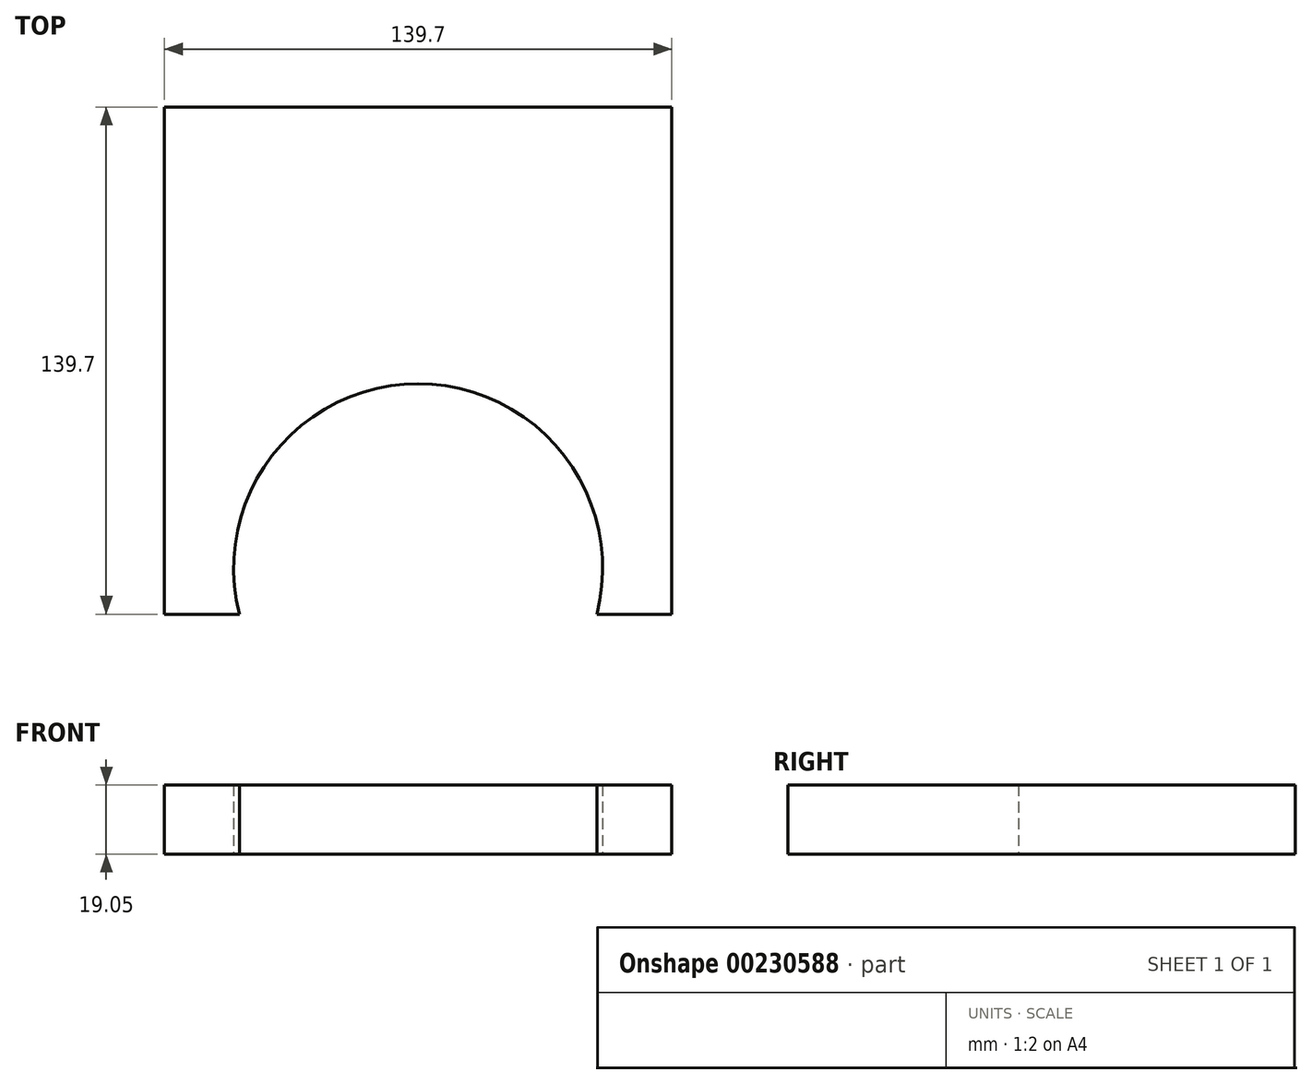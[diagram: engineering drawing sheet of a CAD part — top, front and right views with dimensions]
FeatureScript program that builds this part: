
annotation { "Feature Type Name" : "Feature", "Feature Type Description" : "" }
export const myFeature = defineFeature(function(context is Context, id is Id, definition is map)
    precondition{}
    {
        {
            var Q0;
            Q0=qCreatedBy(makeId("Top.planeOp"),FACE);
            var sketch = newSketch(context, id + "F0", { "sketchPlane" : qUnion([Q0])});
            skLineSegment(sketch, "E0.bottom", {"start": v(-69.85, 69.85) * mm, "end": v(69.85, 69.85) * mm});
            skLineSegment(sketch, "E0.top", {"start": v(-69.85, -69.85) * mm, "end": v(-49.19, -69.85) * mm});
            skLineSegment(sketch, "E0.left", {"start": v(-69.85, 69.85) * mm, "end": v(-69.85, -69.85) * mm});
            skLineSegment(sketch, "E0.right", {"start": v(69.85, 69.85) * mm, "end": v(69.85, -69.85) * mm});
            skPoint(sketch, "E0.middle", {"position": v(0, 0) * mm});
            skArc(sketch, "E1", {"start": v(49.19, -69.85) * mm, "mid": v(0, -6.35) * mm, "end": v(-49.19, -69.85) * mm});
            skLineSegment(sketch, "E2.trimOffspring", {"start": v(49.19, -69.85) * mm, "end": v(69.85, -69.85) * mm});
            skSolve(sketch);
        }
        {
            var Q0;
            Q0=makeQuery(id+"F0.imprint","IMPRINT",FACE,{"disambiguationData":[TD([[makeQuery(id+"F0.imprint","IMPRINT",EDGE,{"derivedFrom":sQuery(id+"F0.wireOp",EDGE,"E0.bottom")}),-1.0]])]});
            extrude(context, id + "F1", {"entities" : qUnion([Q0]), "depth" : 19.05 * mm});
        }
    });
